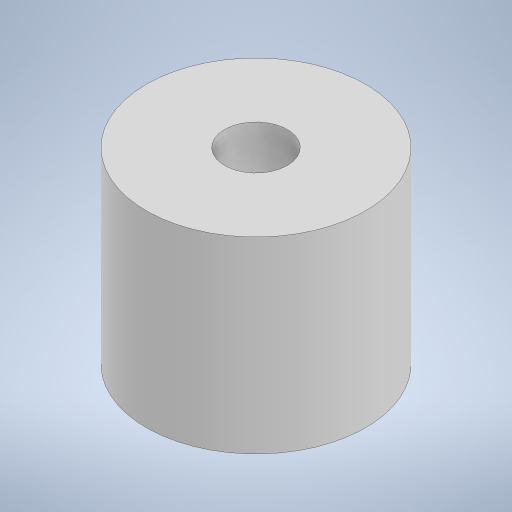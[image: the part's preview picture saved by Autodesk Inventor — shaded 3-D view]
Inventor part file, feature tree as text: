
AUTODESK INVENTOR PART (.ipt)
format: ipt  version: 2024 (Build 280153000, 153)  size: 502,784 bytes
history: native  units: mm
features: extrude x2, sketch x2
ambient origin geometry x8: Origin, YZ Plane, XZ Plane, XY Plane, X Axis, Y Axis, Z Axis, Center Point
bodies: Solid1 (feature_tree)
feature tree (4):
  extrude  "Extrusion1"  Depth=6.0mm TaperAngle=0.0deg
  extrude  "Extrusion2"  Depth=4.0mm TaperAngle=0.0deg
  sketch  "Sketch1"  dims[d0=7.0mm d1=6.0mm d2=0.0mm]
  sketch  "Sketch2"  dims[d3=2.0mm d4=4.0mm d5=0.0mm]
